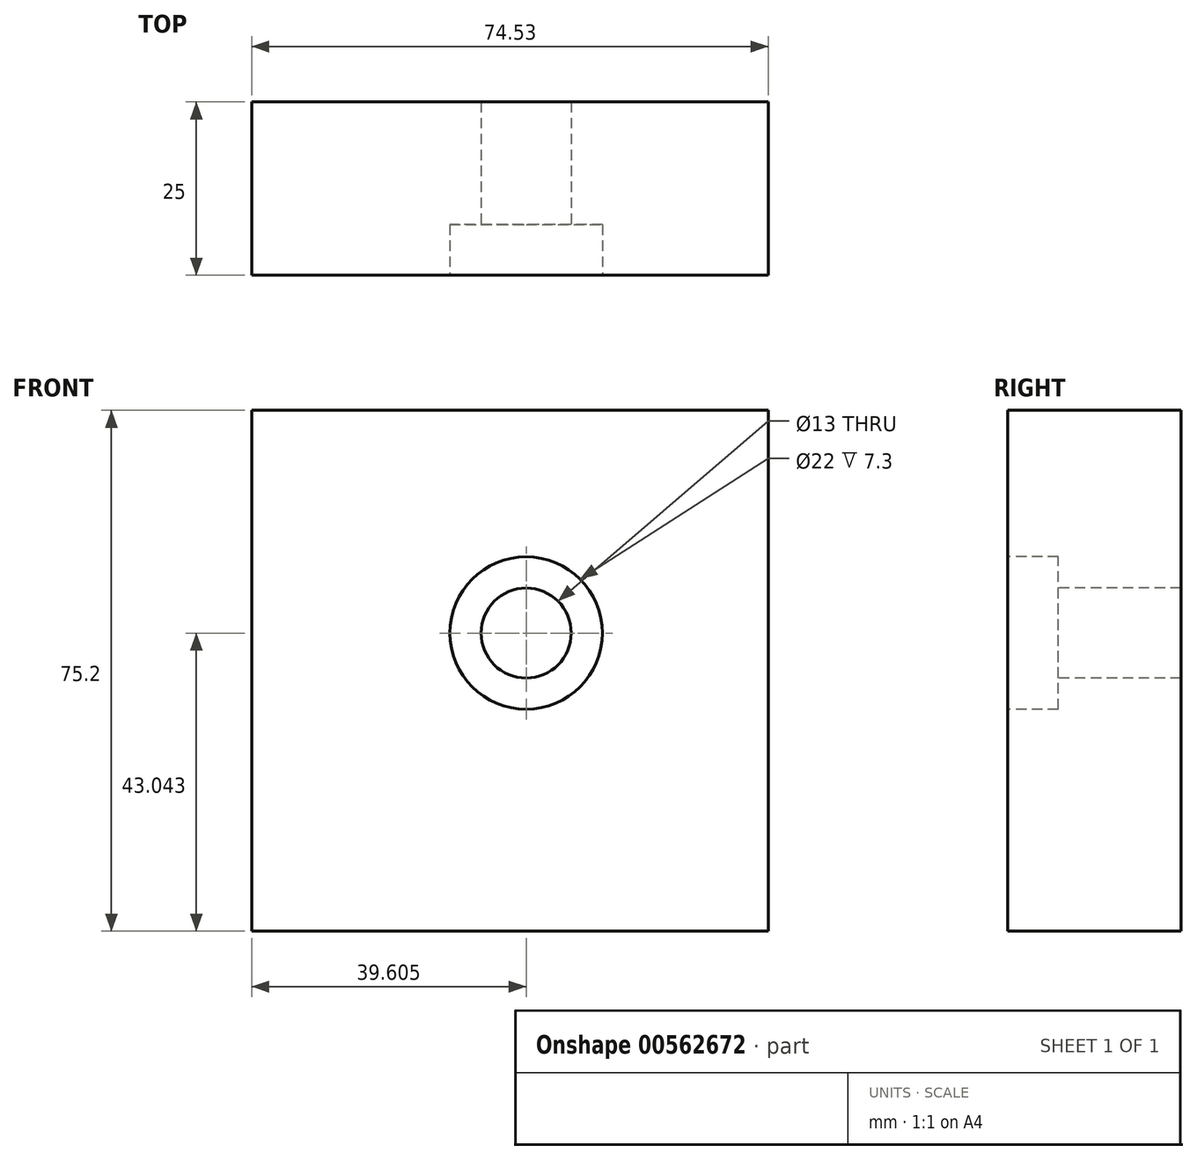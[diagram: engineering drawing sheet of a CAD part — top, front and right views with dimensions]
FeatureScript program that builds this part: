
annotation { "Feature Type Name" : "Feature", "Feature Type Description" : "" }
export const myFeature = defineFeature(function(context is Context, id is Id, definition is map)
    precondition{}
    {
        {
            var Q0;
            Q0=qCreatedBy(makeId("Front.planeOp"),FACE);
            var sketch = newSketch(context, id + "F0", { "sketchPlane" : qUnion([Q0])});
            skLineSegment(sketch, "E0.bottom", {"start": v(-92.73, 53.48) * mm, "end": v(-18.2, 53.48) * mm});
            skLineSegment(sketch, "E0.top", {"start": v(-92.73, -21.72) * mm, "end": v(-18.2, -21.72) * mm});
            skLineSegment(sketch, "E0.left", {"start": v(-92.73, 53.48) * mm, "end": v(-92.73, -21.72) * mm});
            skLineSegment(sketch, "E0.right", {"start": v(-18.2, 53.48) * mm, "end": v(-18.2, -21.72) * mm});
            skSolve(sketch);
        }
        {
            var Q0;
            Q0 = qSketchRegion(id + "F0", true);
            extrude(context, id + "F1", {"entities" : qUnion([Q0]), "depth" : 25 * mm, "offsetDistance" : 25 * mm});
        }
        {
            var Q0;
            Q0=qCreatedBy(makeId("Front.planeOp"),FACE);
            var sketch = newSketch(context, id + "F2", { "sketchPlane" : qUnion([Q0])});
            skLineSegment(sketch, "E1.bottom", {"start": v(119.74, 54.17) * mm, "end": v(176.54, 54.17) * mm});
            skLineSegment(sketch, "E1.top", {"start": v(119.74, 41.23) * mm, "end": v(176.54, 41.23) * mm});
            skLineSegment(sketch, "E1.left", {"start": v(119.74, 54.17) * mm, "end": v(119.74, 41.23) * mm});
            skLineSegment(sketch, "E1.right", {"start": v(176.54, 54.17) * mm, "end": v(176.54, 41.23) * mm});
            skSolve(sketch);
        }
        {
            var Q0;
            Q0=qCreatedBy(makeId("Front.planeOp"),FACE);
            var sketch = newSketch(context, id + "F3", { "sketchPlane" : qUnion([Q0])});
            skLineSegment(sketch, "E2", {"start": v(56.25, -41.91) * mm, "end": v(65.13, -49.22) * mm});
            skSolve(sketch);
        }
        {
            var Q0;
            Q0 = qSketchRegion(id + "F3", true);
            var Q1;
            Q1=sQuery(id+"F3.wireOp",EDGE,"E2");
            extrude(context, id + "F4", {"entities" : qUnion([Q0]), "bodyType" : ToolBodyType.SURFACE, "surfaceEntities" : qUnion([Q1]), "depth" : 25 * mm, "offsetDistance" : 25 * mm});
        }
        {
            var Q0;
            Q0=makeQuery(id+"F1.opExtrude","CAP_FACE",FACE,{"disambiguationData":[OSD([sQuery(id+"F0.wireOp",EDGE,"E0.bottom"),sQuery(id+"F0.wireOp",EDGE,"E0.top"),sQuery(id+"F0.wireOp",EDGE,"E0.left"),sQuery(id+"F0.wireOp",EDGE,"E0.right")])],"isStart":false});
            var sketch = newSketch(context, id + "F5", { "sketchPlane" : qUnion([Q0])});
            skPoint(sketch, "E3", {"position": v(-53.13, 21.32) * mm});
            skSolve(sketch);
        }
        {
            var Q0;
            Q0=sQuery(id+"F5.wireOp",VERTEX,"E3");
            var Q1;
            Q1=makeQuery(id+"F1.opExtrude","SWEPT_BODY",BODY,{"disambiguationData":[OSD([sQuery(id+"F0.wireOp",EDGE,"E0.bottom"),sQuery(id+"F0.wireOp",EDGE,"E0.top"),sQuery(id+"F0.wireOp",EDGE,"E0.left"),sQuery(id+"F0.wireOp",EDGE,"E0.right")])]});
            hole(context, id + "F6", {"style" : HoleStyle.C_BORE, "endStyle" : HoleEndStyle.BLIND, "holeDiameter" : 13 * mm, "cBoreDiameter" : 22 * mm, "cBoreDepth" : 7.3 * mm, "majorDiameter" : 5 * mm, "holeDepth" : 50 * mm, "isTappedThrough" : true, "tappedDepth" : 12 * mm, "tapClearance" : 3, "startFromSketch" : true, "locations" : qUnion([Q0]), "scope" : qUnion([Q1])});
        }
    });
